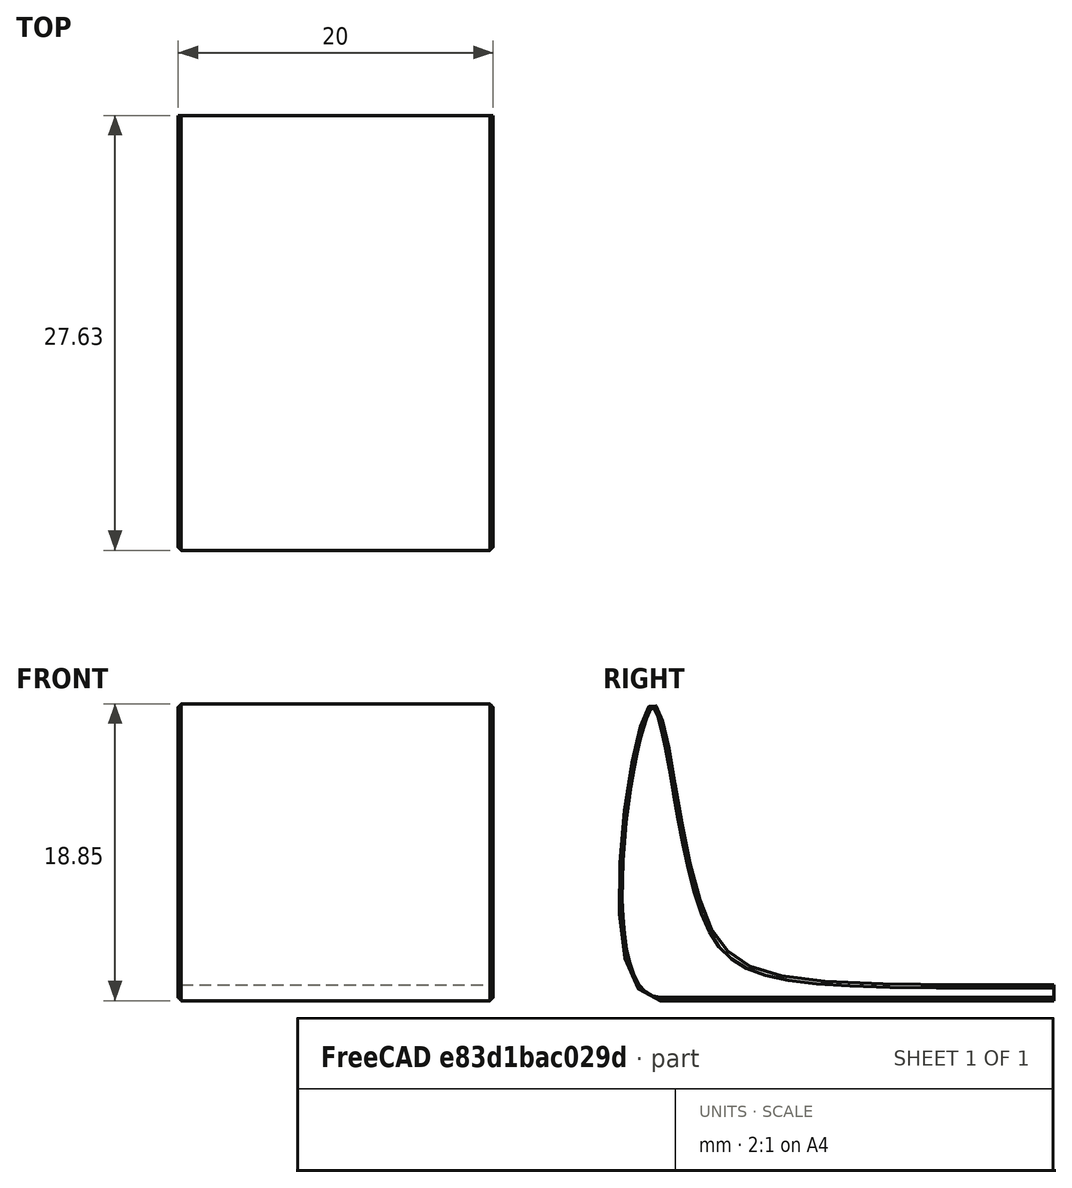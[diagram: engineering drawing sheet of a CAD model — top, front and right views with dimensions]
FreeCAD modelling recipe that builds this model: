
FCSTD DOCUMENT  (FreeCAD 0.19R24291 (Git))
Label: keyboard_stopper
License: All rights reserved
LicenseURL: http://en.wikipedia.org/wiki/All_rights_reserved
objects: PartDesign::Chamfer×2, Sketcher::SketchObject×1, PartDesign::Pad×1, PartDesign::Body×1
note: 8 computed .brp shape members not serialized (recipe doc carries the construction recipe); baked Part::Feature solids carry a one-line shape summary decoded from their .brp

FEATURE [Sketcher::SketchObject] Sketch
  FullyConstrained = false
  MapMode = 5
  Placement = pos=(0,0,0) rot=(0.57735,0.57735,0.57735;2.0944rad)
  Support = -> [YZ_Plane]
  sketch-geometry (12):
    g0: LineSegment StartX=-12.1632 StartY=0 StartZ=0 EndX=12.8368 EndY=0 EndZ=0
    g1-g6: Circle x6 (B-spline internal-alignment scaffolding for g7; pole/knot coordinates omitted)
    g7: BSplineCurve PolesCount=6 KnotsCount=4 Degree=3 IsPeriodic=0
    g8: GeomPoint X=12.8368 Y=1 Z=0
    g9: GeomPoint X=-13.0627 Y=18.4108 Z=0
    g10: GeomPoint X=-12.1632 Y=0 Z=0
    g11: LineSegment StartX=12.8368 StartY=1 StartZ=0 EndX=12.8368 EndY=0 EndZ=0
  constraints (17):
    c: Horizontal(g0)
    c: Weight(g1) = 1
    c: Equal(g1,g2)
    c: Equal(g1,g3)
    c: Equal(g1,g4)
    c: Equal(g1,g6)
    c: InternalAlignment(g1-g6 -> g7) x6
    c: InternalAlignment(g8,g7)
    c: InternalAlignment(g9,g7)
    c: InternalAlignment(g10,g7)
    c: DistanceX(g0,g0) = 25
    c: Tangent(g7,g0) = -1.5708
    c: Horizontal(g0,g-1)
    c: DistanceY(g0,g7) = 1
    c: Coincident(g11,g7)
    c: Coincident(g11,g0)
    c: Vertical(g11)
FEATURE [PartDesign::Pad] Pad
  Direction = (1,1,1)
  Length = 20
  Length2 = 100
  Midplane = true
  Placement = pos=(0,0,0) rot=(0.57735,0.57735,0.57735;2.0944rad)
  Profile = -> Sketch
  Refine = true
  Type = 0
FEATURE [PartDesign::Chamfer] Chamfer
  Angle = 45
  Base = -> Pad [Edge9]
  BaseFeature = -> Pad
  ChamferType = 0
  FlipDirection = false
  Placement = pos=(0,0,0) rot=(0.57735,0.57735,0.57735;2.0944rad)
  Refine = true
  Size = 0.2
  Size2 = 1
  SupportTransform = false
FEATURE [PartDesign::Chamfer] Chamfer001
  Angle = 45
  Base = -> Chamfer [Edge7]
  BaseFeature = -> Chamfer
  ChamferType = 0
  FlipDirection = false
  Placement = pos=(0,0,0) rot=(0.57735,0.57735,0.57735;2.0944rad)
  Refine = true
  Size = 0.2
  Size2 = 1
  SupportTransform = false
FEATURE [PartDesign::Body] Body
  Group = -> [Sketch,Pad,Chamfer,Chamfer001]
  Origin = -> Origin
  Tip = -> Chamfer001
